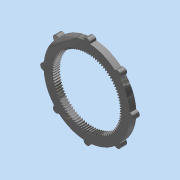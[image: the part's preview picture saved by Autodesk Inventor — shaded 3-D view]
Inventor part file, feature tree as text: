
AUTODESK INVENTOR PART (.ipt)
format: ipt  version: 2015 (Build 190159000, 159)  size: 507,904 bytes
history: native  units: in
note: dims shown in document units (in); Inventor stores cm internally (conversion verified against a paired STEP export)
features: pattern_circular x2, extrude x2, sketch x2, other x1, direct_edit x1, imported_body x1, move_body x1
ambient origin geometry x8: Origin, YZ Plane, XZ Plane, XY Plane, X Axis, Y Axis, Z Axis, Center Point
bodies: Solid1 (feature_tree)
feature tree (10):
  other  "a_1b10-n480961"
  direct_edit  "Direct Edit1"
  pattern_circular  "Circular Pattern1"  Count=48 Angle=360.0deg
  extrude  "Extrusion1"  TaperAngle=0.0deg  [1 undecoded]
  extrude  "Extrusion2"  Depth=1.0in
  pattern_circular  "Circular Pattern2"  [2 undecoded]
  imported_body  "Base1"
  sketch  "Sketch1"  dims[d0=0.0in d1=0.0in d2=0.0625in d3=18.8976in d4=360.0deg]
  sketch  "Sketch2"  dims[d6=2.5591in d7=0.0in d8=0.0in d9=0.1969in d10=1.0in d11=0.0in d12=3.1496in d13=360.0deg]
  move_body  "Move1"
note: 3 required parameter values undecoded (feature->parameter linkage not recoverable at this tier; creation-order binding heuristic only, values carry confidence <= 0.55)
